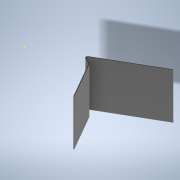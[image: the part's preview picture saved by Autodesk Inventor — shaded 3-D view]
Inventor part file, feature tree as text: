
AUTODESK INVENTOR PART (.ipt)
format: ipt  version: 2022 (Build 260153000, 153)  size: 165,888 bytes
history: native  units: mm
features: sketch x4, sheet_metal_op x3, other x2
ambient origin geometry x8: Origin, YZ Plane, XZ Plane, XY Plane, X Axis, Y Axis, Z Axis, Center Point
bodies: Solid1 (feature_tree)
feature tree (9):
  sheet_metal_op  "Face1"
  sheet_metal_op  "Fold1"
  sheet_metal_op  "Fold2"
  sketch  "Sketch4"  dims[d3=180.0mm d4=20.0mm d5=3.048mm d6=1.524mm d7=6.096mm d8=3.048mm d9=30.0deg d10=3.048mm d11=40.0mm d12=3.048mm d13=1.524mm d14=6.096mm d15=3.048mm d16=120.0deg d17=3.048mm]
  sketch  "Sketch1"  dims[d0=500.0mm]
  other  "Plate1"
  sketch  "Sketch2"  dims[d1=200.0mm]
  sketch  "Sketch3"  dims[d2=3.048mm]
  other  "Definition1"
